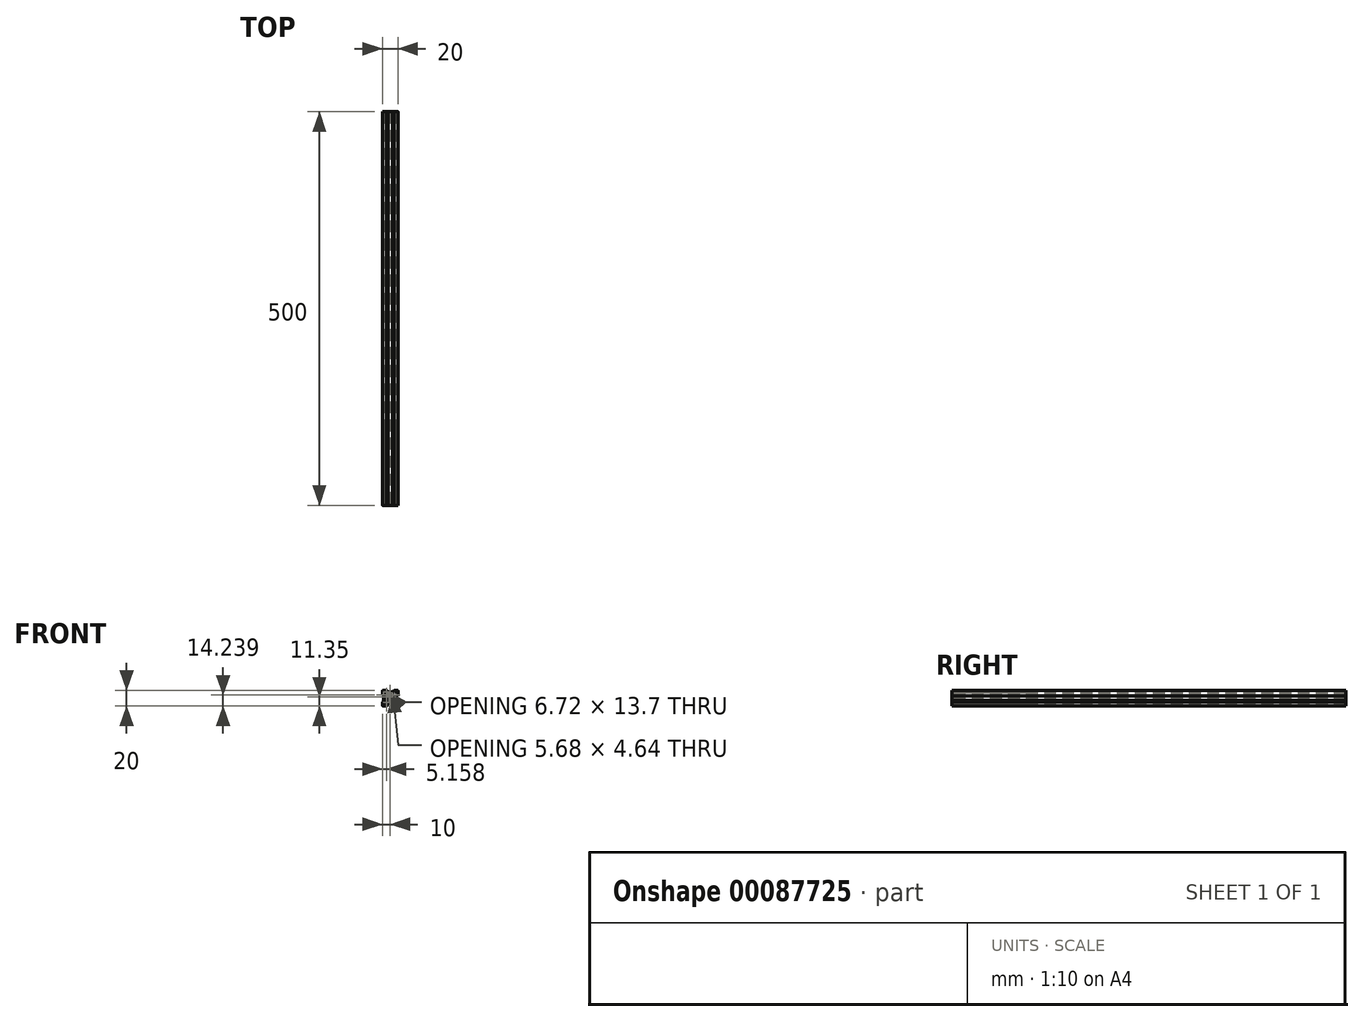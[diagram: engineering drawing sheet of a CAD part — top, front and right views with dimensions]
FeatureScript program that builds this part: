
annotation { "Feature Type Name" : "Feature", "Feature Type Description" : "" }
export const myFeature = defineFeature(function(context is Context, id is Id, definition is map)
    precondition{}
    {
        {
            var Q0;
            Q0=qCreatedBy(makeId("Front.planeOp"),FACE);
            var sketch = newSketch(context, id + "F0", { "sketchPlane" : qUnion([Q0])});
            skLineSegment(sketch, "E0.bottom", {"start": v(0, 0) * mm, "end": v(20, 0) * mm});
            skLineSegment(sketch, "E0.top", {"start": v(0, 20) * mm, "end": v(20, 20) * mm});
            skLineSegment(sketch, "E0.left", {"start": v(0, 0) * mm, "end": v(0, 20) * mm});
            skLineSegment(sketch, "E0.right", {"start": v(20, 0) * mm, "end": v(20, 20) * mm});
            skSolve(sketch);
        }
        {
            var Q0;
            Q0=makeQuery(id+"F0.imprint","IMPRINT",FACE,{"disambiguationData":[TD([[makeQuery(id+"F0.imprint","IMPRINT",EDGE,{"derivedFrom":sQuery(id+"F0.wireOp",EDGE,"E0.bottom")}),1.0]])]});
            extrude(context, id + "F1", {"entities" : qUnion([Q0]), "depth" : 500 * mm});
        }
        {
            var Q0;
            Q0=makeQuery(id+"F1.opExtrude","CAP_FACE",FACE,{"disambiguationData":[OSD([sQuery(id+"F0.wireOp",EDGE,"E0.bottom"),sQuery(id+"F0.wireOp",EDGE,"E0.top"),sQuery(id+"F0.wireOp",EDGE,"E0.left"),sQuery(id+"F0.wireOp",EDGE,"E0.right")])],"isStart":false});
            var sketch = newSketch(context, id + "F2", { "sketchPlane" : qUnion([Q0])});
            skCircle(sketch, "E1", {"center": v(10, 10) * mm, "radius": 2.1 * mm});
            skLineSegment(sketch, "E2", {"start": v(0, 18.94) * mm, "end": v(18.94, 0) * mm});
            skLineSegment(sketch, "E3", {"start": v(20, 1.06) * mm, "end": v(1.06, 20) * mm});
            skLineSegment(sketch, "E4.MirrorCS", {"start": v(20, 18.94) * mm, "end": v(1.06, 0) * mm});
            skLineSegment(sketch, "E5.MirrorCS", {"start": v(0, 1.06) * mm, "end": v(18.94, 20) * mm});
            skLineSegment(sketch, "E6", {"start": v(18.2, 1.8) * mm, "end": v(18.2, 18.2) * mm});
            skLineSegment(sketch, "E7.bottom", {"start": v(1.8, 18.2) * mm, "end": v(18.2, 18.2) * mm});
            skLineSegment(sketch, "E7.left", {"start": v(1.8, 18.2) * mm, "end": v(1.8, 1.8) * mm});
            skLineSegment(sketch, "E7.right", {"start": v(18.2, 18.2) * mm, "end": v(18.2, 1.8) * mm});
            skLineSegment(sketch, "E8", {"start": v(1.8, 1.8) * mm, "end": v(18.2, 1.8) * mm});
            skLineSegment(sketch, "E9", {"start": v(10, 10) * mm, "end": v(10, 0) * mm});
            skLineSegment(sketch, "E10", {"start": v(10, 0) * mm, "end": v(7.16, 0) * mm});
            skLineSegment(sketch, "E11", {"start": v(10, 0) * mm, "end": v(12.84, 0) * mm});
            skLineSegment(sketch, "E12", {"start": v(7.16, 0) * mm, "end": v(7.16, 6.1) * mm});
            skLineSegment(sketch, "E13", {"start": v(12.84, 0) * mm, "end": v(12.84, 6.1) * mm});
            skLineSegment(sketch, "E14", {"start": v(12.84, 6.1) * mm, "end": v(7.16, 6.1) * mm});
            skLineSegment(sketch, "E15", {"start": v(7.16, 1.8) * mm, "end": v(5.36, 0) * mm});
            skLineSegment(sketch, "E16", {"start": v(12.84, 0) * mm, "end": v(14.64, 0) * mm});
            skLineSegment(sketch, "E17", {"start": v(14.64, 0) * mm, "end": v(12.84, 1.8) * mm});
            skLineSegment(sketch, "E18", {"start": v(7.16, 1.8) * mm, "end": v(7.16, 3.44) * mm});
            skLineSegment(sketch, "E19", {"start": v(4.5, 3.44) * mm, "end": v(15.5, 3.44) * mm});
            skLineSegment(sketch, "E20", {"start": v(15.5, 3.44) * mm, "end": v(15.5, 0) * mm});
            skLineSegment(sketch, "E21", {"start": v(4.5, 3.44) * mm, "end": v(4.5, 0) * mm});
            skLineSegment(sketch, "E22.MirrorCS", {"start": v(14.64, 20) * mm, "end": v(12.84, 18.2) * mm});
            skLineSegment(sketch, "E23.MirrorCS", {"start": v(15.5, 16.56) * mm, "end": v(15.5, 20) * mm});
            skLineSegment(sketch, "E24.MirrorCS", {"start": v(7.16, 20) * mm, "end": v(7.16, 13.9) * mm});
            skLineSegment(sketch, "E25.MirrorCS", {"start": v(4.5, 16.56) * mm, "end": v(4.5, 20) * mm});
            skLineSegment(sketch, "E26.MirrorCS", {"start": v(10, 10) * mm, "end": v(10, 20) * mm});
            skLineSegment(sketch, "E27.MirrorCS", {"start": v(12.84, 13.9) * mm, "end": v(7.16, 13.9) * mm});
            skLineSegment(sketch, "E28.MirrorCS", {"start": v(12.84, 20) * mm, "end": v(14.64, 20) * mm});
            skLineSegment(sketch, "E29.MirrorCS", {"start": v(10, 20) * mm, "end": v(12.84, 20) * mm});
            skLineSegment(sketch, "E30.MirrorCS", {"start": v(10, 20) * mm, "end": v(7.16, 20) * mm});
            skLineSegment(sketch, "E31.MirrorCS", {"start": v(1.8, 1.8) * mm, "end": v(1.8, 18.2) * mm});
            skLineSegment(sketch, "E32.MirrorCS", {"start": v(12.84, 20) * mm, "end": v(12.84, 13.9) * mm});
            skLineSegment(sketch, "E33.MirrorCS", {"start": v(4.5, 16.56) * mm, "end": v(15.5, 16.56) * mm});
            skLineSegment(sketch, "E34.MirrorCS", {"start": v(7.16, 18.2) * mm, "end": v(5.36, 20) * mm});
            skLineSegment(sketch, "E35.MirrorCS", {"start": v(12.84, 1.8) * mm, "end": v(12.84, 3.44) * mm});
            skLineSegment(sketch, "E36.MirrorCS", {"start": v(12.84, 18.2) * mm, "end": v(12.84, 16.56) * mm});
            skLineSegment(sketch, "E37.MirrorCS", {"start": v(12.84, 1.8) * mm, "end": v(14.64, 0) * mm});
            skLineSegment(sketch, "E38.MirrorCS", {"start": v(12.84, 18.2) * mm, "end": v(14.64, 20) * mm});
            skLineSegment(sketch, "E39.MirrorCS", {"start": v(7.16, 6.1) * mm, "end": v(12.84, 6.1) * mm});
            skLineSegment(sketch, "E40.MirrorCS", {"start": v(15.5, 3.44) * mm, "end": v(4.5, 3.44) * mm});
            skLineSegment(sketch, "E41.MirrorCS", {"start": v(18.2, 1.8) * mm, "end": v(1.8, 1.8) * mm});
            skLineSegment(sketch, "E42.MirrorCS", {"start": v(7.16, 0) * mm, "end": v(5.36, 0) * mm});
            skLineSegment(sketch, "E43.MirrorCS", {"start": v(5.36, 0) * mm, "end": v(7.16, 1.8) * mm});
            skLineSegment(sketch, "E44", {"start": v(0, 20) * mm, "end": v(20, 0) * mm});
            skLineSegment(sketch, "E45.MirrorCS", {"start": v(3.44, 4.5) * mm, "end": v(0, 4.5) * mm});
            skLineSegment(sketch, "E46.MirrorCS", {"start": v(0, 10) * mm, "end": v(0, 7.16) * mm});
            skLineSegment(sketch, "E47.MirrorCS", {"start": v(0, 5.36) * mm, "end": v(1.8, 7.16) * mm});
            skLineSegment(sketch, "E48.MirrorCS", {"start": v(0, 7.16) * mm, "end": v(6.1, 7.16) * mm});
            skLineSegment(sketch, "E49.MirrorCS", {"start": v(1.8, 7.16) * mm, "end": v(3.44, 7.16) * mm});
            skLineSegment(sketch, "E50.MirrorCS", {"start": v(3.44, 15.5) * mm, "end": v(0, 15.5) * mm});
            skLineSegment(sketch, "E51.MirrorCS", {"start": v(0, 10) * mm, "end": v(0, 12.84) * mm});
            skLineSegment(sketch, "E52.MirrorCS", {"start": v(1.8, 12.84) * mm, "end": v(0, 14.64) * mm});
            skLineSegment(sketch, "E53.MirrorCS", {"start": v(0, 7.16) * mm, "end": v(0, 5.36) * mm});
            skLineSegment(sketch, "E54.MirrorCS", {"start": v(0, 12.84) * mm, "end": v(6.1, 12.84) * mm});
            skLineSegment(sketch, "E55.MirrorCS", {"start": v(6.1, 7.16) * mm, "end": v(6.1, 12.84) * mm});
            skLineSegment(sketch, "E56.MirrorCS", {"start": v(1.8, 7.16) * mm, "end": v(0, 5.36) * mm});
            skLineSegment(sketch, "E57.MirrorCS", {"start": v(1.8, 12.84) * mm, "end": v(3.44, 12.84) * mm});
            skLineSegment(sketch, "E58.MirrorCS", {"start": v(3.44, 15.5) * mm, "end": v(3.44, 4.5) * mm});
            skLineSegment(sketch, "E59.MirrorCS", {"start": v(18.2, 18.2) * mm, "end": v(1.8, 18.2) * mm});
            skLineSegment(sketch, "E60.MirrorCS", {"start": v(7.16, 18.2) * mm, "end": v(7.16, 16.56) * mm});
            skLineSegment(sketch, "E61.MirrorCS", {"start": v(18.2, 12.84) * mm, "end": v(16.56, 12.84) * mm});
            skLineSegment(sketch, "E62.MirrorCS", {"start": v(20, 7.16) * mm, "end": v(13.9, 7.16) * mm});
            skLineSegment(sketch, "E63.MirrorCS", {"start": v(18.2, 7.16) * mm, "end": v(16.56, 7.16) * mm});
            skLineSegment(sketch, "E64.MirrorCS", {"start": v(20, 12.84) * mm, "end": v(13.9, 12.84) * mm});
            skLineSegment(sketch, "E65.MirrorCS", {"start": v(16.56, 15.5) * mm, "end": v(20, 15.5) * mm});
            skLineSegment(sketch, "E66.MirrorCS", {"start": v(20, 14.64) * mm, "end": v(18.2, 12.84) * mm});
            skLineSegment(sketch, "E67.MirrorCS", {"start": v(20, 10) * mm, "end": v(20, 12.84) * mm});
            skLineSegment(sketch, "E68.MirrorCS", {"start": v(16.56, 4.5) * mm, "end": v(20, 4.5) * mm});
            skLineSegment(sketch, "E69.MirrorCS", {"start": v(20, 10) * mm, "end": v(20, 7.16) * mm});
            skLineSegment(sketch, "E70.MirrorCS", {"start": v(18.2, 7.16) * mm, "end": v(20, 5.36) * mm});
            skLineSegment(sketch, "E71.MirrorCS", {"start": v(13.9, 12.84) * mm, "end": v(13.9, 7.16) * mm});
            skLineSegment(sketch, "E72.MirrorCS", {"start": v(20, 5.36) * mm, "end": v(18.2, 7.16) * mm});
            skLineSegment(sketch, "E73.MirrorCS", {"start": v(16.56, 4.5) * mm, "end": v(16.56, 15.5) * mm});
            skLineSegment(sketch, "E74.MirrorCS", {"start": v(18.2, 12.84) * mm, "end": v(20, 14.64) * mm});
            skLineSegment(sketch, "E75.MirrorCS", {"start": v(13.9, 7.16) * mm, "end": v(13.9, 12.84) * mm});
            skLineSegment(sketch, "E76.MirrorCS", {"start": v(20, 7.16) * mm, "end": v(20, 5.36) * mm});
            skLineSegment(sketch, "E77.MirrorCS", {"start": v(16.56, 15.5) * mm, "end": v(16.56, 4.5) * mm});
            skLineSegment(sketch, "E78.MirrorCS", {"start": v(20, 12.84) * mm, "end": v(20, 14.64) * mm});
            skLineSegment(sketch, "E79", {"start": v(7.16, 18.2) * mm, "end": v(4.5, 18.2) * mm});
            skSolve(sketch);
        }
        {
            var Q0;
            {var subQ0=sQuery(id+"F2.wireOp",EDGE,"E55.MirrorCS");Q0=makeQuery(id+"F2.imprint","IMPRINT",FACE,{"disambiguationData":[TD([[makeQuery(id+"F2.imprint","IMPRINT",EDGE,{"derivedFrom":subQ0}),1.0]])]});}
            var Q1;
            {var subQ0=sQuery(id+"F2.wireOp",EDGE,"E58.MirrorCS");var subQ1=sQuery(id+"F2.wireOp",EDGE,"E2");var subQ2=makeQuery(id+"F2.imprint","INTERSECT",VERTEX,{"derivedFrom":[subQ1,sQuery(id+"F2.wireOp",EDGE,"E50.MirrorCS"),subQ0]});Q1=makeQuery(id+"F2.imprint","IMPRINT",FACE,{"disambiguationData":[TD([[makeQuery(id+"F2.imprint","IMPRINT",EDGE,{"disambiguationData":[TD([[subQ2,-1.0]])],"derivedFrom":subQ1}),-1.0]])]});}
            var Q2;
            {var subQ5=sQuery(id+"F2.wireOp",EDGE,"E57.MirrorCS");Q2=makeQuery(id+"F2.imprint","IMPRINT",FACE,{"disambiguationData":[TD([[makeQuery(id+"F2.imprint","IMPRINT",EDGE,{"derivedFrom":subQ5}),1.0]])]});}
            var Q3;
            {var subQ0=sQuery(id+"F2.wireOp",EDGE,"E57.MirrorCS");Q3=makeQuery(id+"F2.imprint","IMPRINT",FACE,{"disambiguationData":[TD([[makeQuery(id+"F2.imprint","IMPRINT",EDGE,{"derivedFrom":subQ0}),-1.0]])]});}
            var Q4;
            {var subQ4=sQuery(id+"F2.wireOp",EDGE,"E46.MirrorCS");Q4=makeQuery(id+"F2.imprint","IMPRINT",FACE,{"disambiguationData":[TD([[makeQuery(id+"F2.imprint","IMPRINT",EDGE,{"derivedFrom":subQ4}),-1.0]])]});}
            var Q5;
            {var subQ0=sQuery(id+"F2.wireOp",EDGE,"E52.MirrorCS");Q5=makeQuery(id+"F2.imprint","IMPRINT",FACE,{"disambiguationData":[TD([[makeQuery(id+"F2.imprint","IMPRINT",EDGE,{"derivedFrom":subQ0}),1.0]])]});}
            var Q6;
            {var subQ0=sQuery(id+"F2.wireOp",EDGE,"E53.MirrorCS");Q6=makeQuery(id+"F2.imprint","IMPRINT",FACE,{"disambiguationData":[TD([[makeQuery(id+"F2.imprint","IMPRINT",EDGE,{"derivedFrom":subQ0}),-1.0]])]});}
            var Q7;
            {var subQ1=sQuery(id+"F2.wireOp",EDGE,"E45.MirrorCS");var subQ3=sQuery(id+"F2.wireOp",EDGE,"E7.left");var subQ4=makeQuery(id+"F2.imprint","INTERSECT",VERTEX,{"derivedFrom":[subQ1,subQ3]});Q7=makeQuery(id+"F2.imprint","IMPRINT",FACE,{"disambiguationData":[TD([[makeQuery(id+"F2.imprint","IMPRINT",EDGE,{"disambiguationData":[TD([[subQ4,1.0]])],"derivedFrom":subQ1}),-1.0]])]});}
            var Q8;
            {var subQ0=sQuery(id+"F2.wireOp",EDGE,"E58.MirrorCS");var subQ3=sQuery(id+"F2.wireOp",EDGE,"E48.MirrorCS");var subQ5=makeQuery(id+"F2.imprint","INTERSECT",VERTEX,{"derivedFrom":[subQ0,subQ3]});Q8=makeQuery(id+"F2.imprint","IMPRINT",FACE,{"disambiguationData":[TD([[makeQuery(id+"F2.imprint","IMPRINT",EDGE,{"disambiguationData":[TD([[subQ5,-1.0]])],"derivedFrom":subQ0}),1.0]])]});}
            var Q9;
            {var subQ0=sQuery(id+"F2.wireOp",EDGE,"E27.MirrorCS");var subQ5=sQuery(id+"F2.wireOp",EDGE,"E26.MirrorCS");var subQ6=makeQuery(id+"F2.imprint","INTERSECT",VERTEX,{"derivedFrom":[subQ5,subQ0]});Q9=makeQuery(id+"F2.imprint","IMPRINT",FACE,{"disambiguationData":[TD([[makeQuery(id+"F2.imprint","IMPRINT",EDGE,{"disambiguationData":[TD([[subQ6,-1.0]])],"derivedFrom":subQ5}),1.0]])]});}
            var Q10;
            {var subQ0=sQuery(id+"F2.wireOp",EDGE,"E24.MirrorCS");var subQ1=sQuery(id+"F2.wireOp",EDGE,"E3");var subQ2=makeQuery(id+"F2.imprint","INTERSECT",VERTEX,{"derivedFrom":[subQ1,subQ0,sQuery(id+"F2.wireOp",EDGE,"E27.MirrorCS")]});Q10=makeQuery(id+"F2.imprint","IMPRINT",FACE,{"disambiguationData":[TD([[makeQuery(id+"F2.imprint","IMPRINT",EDGE,{"disambiguationData":[TD([[subQ2,-1.0]])],"derivedFrom":subQ1}),-1.0]])]});}
            var Q11;
            {var subQ0=sQuery(id+"F2.wireOp",EDGE,"E27.MirrorCS");var subQ1=sQuery(id+"F2.wireOp",EDGE,"E26.MirrorCS");var subQ2=makeQuery(id+"F2.imprint","INTERSECT",VERTEX,{"derivedFrom":[subQ1,subQ0]});Q11=makeQuery(id+"F2.imprint","IMPRINT",FACE,{"disambiguationData":[TD([[makeQuery(id+"F2.imprint","IMPRINT",EDGE,{"disambiguationData":[TD([[subQ2,-1.0]])],"derivedFrom":subQ1}),-1.0]])]});}
            var Q12;
            {var subQ0=sQuery(id+"F2.wireOp",EDGE,"E32.MirrorCS");var subQ1=sQuery(id+"F2.wireOp",EDGE,"E5.MirrorCS");var subQ2=makeQuery(id+"F2.imprint","INTERSECT",VERTEX,{"derivedFrom":[sQuery(id+"F2.wireOp",EDGE,"E27.MirrorCS"),subQ1,subQ0]});Q12=makeQuery(id+"F2.imprint","IMPRINT",FACE,{"disambiguationData":[TD([[makeQuery(id+"F2.imprint","IMPRINT",EDGE,{"disambiguationData":[TD([[subQ2,-1.0]])],"derivedFrom":subQ1}),1.0]])]});}
            var Q13;
            {var subQ0=sQuery(id+"F2.wireOp",EDGE,"E36.MirrorCS");Q13=makeQuery(id+"F2.imprint","IMPRINT",FACE,{"disambiguationData":[TD([[makeQuery(id+"F2.imprint","IMPRINT",EDGE,{"derivedFrom":subQ0}),1.0]])]});}
            var Q14;
            {var subQ5=sQuery(id+"F2.wireOp",EDGE,"E36.MirrorCS");Q14=makeQuery(id+"F2.imprint","IMPRINT",FACE,{"disambiguationData":[TD([[makeQuery(id+"F2.imprint","IMPRINT",EDGE,{"derivedFrom":subQ5}),-1.0]])]});}
            var Q15;
            {var subQ5=sQuery(id+"F2.wireOp",EDGE,"E60.MirrorCS");Q15=makeQuery(id+"F2.imprint","IMPRINT",FACE,{"disambiguationData":[TD([[makeQuery(id+"F2.imprint","IMPRINT",EDGE,{"derivedFrom":subQ5}),1.0]])]});}
            var Q16;
            {var subQ0=sQuery(id+"F2.wireOp",EDGE,"E60.MirrorCS");Q16=makeQuery(id+"F2.imprint","IMPRINT",FACE,{"disambiguationData":[TD([[makeQuery(id+"F2.imprint","IMPRINT",EDGE,{"derivedFrom":subQ0}),-1.0]])]});}
            var Q17;
            {var subQ3=sQuery(id+"F2.wireOp",EDGE,"E34.MirrorCS");Q17=makeQuery(id+"F2.imprint","IMPRINT",FACE,{"disambiguationData":[TD([[makeQuery(id+"F2.imprint","IMPRINT",EDGE,{"derivedFrom":subQ3}),-1.0]])]});}
            var Q18;
            {var subQ0=sQuery(id+"F2.wireOp",EDGE,"E30.MirrorCS");Q18=makeQuery(id+"F2.imprint","IMPRINT",FACE,{"disambiguationData":[TD([[makeQuery(id+"F2.imprint","IMPRINT",EDGE,{"derivedFrom":subQ0}),-1.0]])]});}
            var Q19;
            {var subQ0=sQuery(id+"F2.wireOp",EDGE,"E29.MirrorCS");Q19=makeQuery(id+"F2.imprint","IMPRINT",FACE,{"disambiguationData":[TD([[makeQuery(id+"F2.imprint","IMPRINT",EDGE,{"derivedFrom":subQ0}),-1.0]])]});}
            var Q20;
            {var subQ2=sQuery(id+"F2.wireOp",EDGE,"E22.MirrorCS");Q20=makeQuery(id+"F2.imprint","IMPRINT",FACE,{"disambiguationData":[TD([[makeQuery(id+"F2.imprint","IMPRINT",EDGE,{"derivedFrom":subQ2}),-1.0]])]});}
            var Q21;
            {var subQ0=sQuery(id+"F2.wireOp",EDGE,"E64.MirrorCS");var subQ3=sQuery(id+"F2.wireOp",EDGE,"E77.MirrorCS");var subQ5=makeQuery(id+"F2.imprint","INTERSECT",VERTEX,{"derivedFrom":[subQ3,subQ0]});Q21=makeQuery(id+"F2.imprint","IMPRINT",FACE,{"disambiguationData":[TD([[makeQuery(id+"F2.imprint","IMPRINT",EDGE,{"disambiguationData":[TD([[subQ5,1.0]])],"derivedFrom":subQ3}),-1.0]])]});}
            var Q22;
            {var subQ0=sQuery(id+"F2.wireOp",EDGE,"E75.MirrorCS");Q22=makeQuery(id+"F2.imprint","IMPRINT",FACE,{"disambiguationData":[TD([[makeQuery(id+"F2.imprint","IMPRINT",EDGE,{"derivedFrom":subQ0}),-1.0]])]});}
            var Q23;
            {var subQ0=sQuery(id+"F2.wireOp",EDGE,"E63.MirrorCS");Q23=makeQuery(id+"F2.imprint","IMPRINT",FACE,{"disambiguationData":[TD([[makeQuery(id+"F2.imprint","IMPRINT",EDGE,{"derivedFrom":subQ0}),-1.0]])]});}
            var Q24;
            {var subQ1=sQuery(id+"F2.wireOp",EDGE,"E77.MirrorCS");var subQ3=sQuery(id+"F2.wireOp",EDGE,"E64.MirrorCS");var subQ4=makeQuery(id+"F2.imprint","INTERSECT",VERTEX,{"derivedFrom":[subQ1,subQ3]});Q24=makeQuery(id+"F2.imprint","IMPRINT",FACE,{"disambiguationData":[TD([[makeQuery(id+"F2.imprint","IMPRINT",EDGE,{"disambiguationData":[TD([[subQ4,1.0]])],"derivedFrom":subQ1}),1.0]])]});}
            var Q25;
            {var subQ0=sQuery(id+"F2.wireOp",EDGE,"E74.MirrorCS");Q25=makeQuery(id+"F2.imprint","IMPRINT",FACE,{"disambiguationData":[TD([[makeQuery(id+"F2.imprint","IMPRINT",EDGE,{"derivedFrom":subQ0}),-1.0]])]});}
            var Q26;
            {var subQ6=sQuery(id+"F2.wireOp",EDGE,"E67.MirrorCS");Q26=makeQuery(id+"F2.imprint","IMPRINT",FACE,{"disambiguationData":[TD([[makeQuery(id+"F2.imprint","IMPRINT",EDGE,{"derivedFrom":subQ6}),1.0]])]});}
            var Q27;
            {var subQ0=sQuery(id+"F2.wireOp",EDGE,"E76.MirrorCS");Q27=makeQuery(id+"F2.imprint","IMPRINT",FACE,{"disambiguationData":[TD([[makeQuery(id+"F2.imprint","IMPRINT",EDGE,{"derivedFrom":subQ0}),1.0]])]});}
            var Q28;
            {var subQ3=sQuery(id+"F2.wireOp",EDGE,"E63.MirrorCS");Q28=makeQuery(id+"F2.imprint","IMPRINT",FACE,{"disambiguationData":[TD([[makeQuery(id+"F2.imprint","IMPRINT",EDGE,{"derivedFrom":subQ3}),1.0]])]});}
            var Q29;
            {var subQ0=sQuery(id+"F2.wireOp",EDGE,"E62.MirrorCS");var subQ1=sQuery(id+"F2.wireOp",EDGE,"E3");var subQ2=makeQuery(id+"F2.imprint","INTERSECT",VERTEX,{"derivedFrom":[subQ1,sQuery(id+"F2.wireOp",EDGE,"E75.MirrorCS"),subQ0]});Q29=makeQuery(id+"F2.imprint","IMPRINT",FACE,{"disambiguationData":[TD([[makeQuery(id+"F2.imprint","IMPRINT",EDGE,{"disambiguationData":[TD([[subQ2,1.0]])],"derivedFrom":subQ1}),-1.0]])]});}
            var Q30;
            {var subQ0=sQuery(id+"F2.wireOp",EDGE,"E16");Q30=makeQuery(id+"F2.imprint","IMPRINT",FACE,{"disambiguationData":[TD([[makeQuery(id+"F2.imprint","IMPRINT",EDGE,{"derivedFrom":subQ0}),1.0]])]});}
            var Q31;
            {var subQ0=sQuery(id+"F2.wireOp",EDGE,"E11");Q31=makeQuery(id+"F2.imprint","IMPRINT",FACE,{"disambiguationData":[TD([[makeQuery(id+"F2.imprint","IMPRINT",EDGE,{"derivedFrom":subQ0}),1.0]])]});}
            var Q32;
            {var subQ0=sQuery(id+"F2.wireOp",EDGE,"E10");Q32=makeQuery(id+"F2.imprint","IMPRINT",FACE,{"disambiguationData":[TD([[makeQuery(id+"F2.imprint","IMPRINT",EDGE,{"derivedFrom":subQ0}),1.0]])]});}
            var Q33;
            {var subQ0=sQuery(id+"F2.wireOp",EDGE,"E42.MirrorCS");Q33=makeQuery(id+"F2.imprint","IMPRINT",FACE,{"disambiguationData":[TD([[makeQuery(id+"F2.imprint","IMPRINT",EDGE,{"derivedFrom":subQ0}),1.0]])]});}
            var Q34;
            {var subQ1=sQuery(id+"F2.wireOp",EDGE,"E40.MirrorCS");var subQ3=sQuery(id+"F2.wireOp",EDGE,"E12");var subQ4=makeQuery(id+"F2.imprint","INTERSECT",VERTEX,{"derivedFrom":[subQ1,subQ3]});Q34=makeQuery(id+"F2.imprint","IMPRINT",FACE,{"disambiguationData":[TD([[makeQuery(id+"F2.imprint","IMPRINT",EDGE,{"disambiguationData":[TD([[subQ4,-1.0]])],"derivedFrom":subQ1}),1.0]])]});}
            var Q35;
            {var subQ0=sQuery(id+"F2.wireOp",EDGE,"E12");var subQ3=sQuery(id+"F2.wireOp",EDGE,"E40.MirrorCS");var subQ5=makeQuery(id+"F2.imprint","INTERSECT",VERTEX,{"derivedFrom":[subQ3,subQ0]});Q35=makeQuery(id+"F2.imprint","IMPRINT",FACE,{"disambiguationData":[TD([[makeQuery(id+"F2.imprint","IMPRINT",EDGE,{"disambiguationData":[TD([[subQ5,-1.0]])],"derivedFrom":subQ3}),-1.0]])]});}
            var Q36;
            {var subQ0=sQuery(id+"F2.wireOp",EDGE,"E39.MirrorCS");var subQ1=sQuery(id+"F2.wireOp",EDGE,"E9");var subQ2=makeQuery(id+"F2.imprint","INTERSECT",VERTEX,{"derivedFrom":[subQ1,subQ0]});Q36=makeQuery(id+"F2.imprint","IMPRINT",FACE,{"disambiguationData":[TD([[makeQuery(id+"F2.imprint","IMPRINT",EDGE,{"disambiguationData":[TD([[subQ2,-1.0]])],"derivedFrom":subQ1}),-1.0]])]});}
            var Q37;
            {var subQ0=sQuery(id+"F2.wireOp",EDGE,"E39.MirrorCS");var subQ1=sQuery(id+"F2.wireOp",EDGE,"E9");var subQ2=makeQuery(id+"F2.imprint","INTERSECT",VERTEX,{"derivedFrom":[subQ1,subQ0]});Q37=makeQuery(id+"F2.imprint","IMPRINT",FACE,{"disambiguationData":[TD([[makeQuery(id+"F2.imprint","IMPRINT",EDGE,{"disambiguationData":[TD([[subQ2,-1.0]])],"derivedFrom":subQ1}),1.0]])]});}
            var Q38;
            {var subQ0=sQuery(id+"F2.wireOp",EDGE,"E13");var subQ3=sQuery(id+"F2.wireOp",EDGE,"E40.MirrorCS");var subQ5=makeQuery(id+"F2.imprint","INTERSECT",VERTEX,{"derivedFrom":[subQ3,subQ0]});Q38=makeQuery(id+"F2.imprint","IMPRINT",FACE,{"disambiguationData":[TD([[makeQuery(id+"F2.imprint","IMPRINT",EDGE,{"disambiguationData":[TD([[subQ5,1.0]])],"derivedFrom":subQ3}),-1.0]])]});}
            var Q39;
            {var subQ1=sQuery(id+"F2.wireOp",EDGE,"E20");var subQ3=sQuery(id+"F2.wireOp",EDGE,"E41.MirrorCS");var subQ4=makeQuery(id+"F2.imprint","INTERSECT",VERTEX,{"derivedFrom":[subQ1,subQ3]});Q39=makeQuery(id+"F2.imprint","IMPRINT",FACE,{"disambiguationData":[TD([[makeQuery(id+"F2.imprint","IMPRINT",EDGE,{"disambiguationData":[TD([[subQ4,1.0]])],"derivedFrom":subQ1}),-1.0]])]});}
            var Q40;
            {var subQ0=sQuery(id+"F2.wireOp",EDGE,"E40.MirrorCS");var subQ1=sQuery(id+"F2.wireOp",EDGE,"E9");var subQ2=makeQuery(id+"F2.imprint","INTERSECT",VERTEX,{"derivedFrom":[subQ1,subQ0]});Q40=makeQuery(id+"F2.imprint","IMPRINT",FACE,{"disambiguationData":[TD([[makeQuery(id+"F2.imprint","IMPRINT",EDGE,{"disambiguationData":[TD([[subQ2,-1.0]])],"derivedFrom":subQ1}),1.0]])]});}
            var Q41;
            {var subQ0=sQuery(id+"F2.wireOp",EDGE,"E40.MirrorCS");var subQ1=sQuery(id+"F2.wireOp",EDGE,"E9");var subQ2=makeQuery(id+"F2.imprint","INTERSECT",VERTEX,{"derivedFrom":[subQ1,subQ0]});Q41=makeQuery(id+"F2.imprint","IMPRINT",FACE,{"disambiguationData":[TD([[makeQuery(id+"F2.imprint","IMPRINT",EDGE,{"disambiguationData":[TD([[subQ2,-1.0]])],"derivedFrom":subQ1}),-1.0]])]});}
            var Q42;
            {var subQ0=sQuery(id+"F2.wireOp",EDGE,"E2");var subQ1=sQuery(id+"F2.wireOp",EDGE,"E1");var subQ2=makeQuery(id+"F2.imprint","INTERSECT",VERTEX,{"disambiguationData":[OD(1.0)],"derivedFrom":[subQ1,subQ0]});Q42=makeQuery(id+"F2.imprint","IMPRINT",FACE,{"disambiguationData":[TD([[makeQuery(id+"F2.imprint","IMPRINT",EDGE,{"disambiguationData":[TD([[subQ2,-1.0]])],"derivedFrom":subQ1}),-1.0]])]});}
            var Q43;
            {var subQ0=sQuery(id+"F2.wireOp",EDGE,"E9");var subQ1=sQuery(id+"F2.wireOp",EDGE,"E1");var subQ2=makeQuery(id+"F2.imprint","INTERSECT",VERTEX,{"derivedFrom":[subQ1,subQ0]});Q43=makeQuery(id+"F2.imprint","IMPRINT",FACE,{"disambiguationData":[TD([[makeQuery(id+"F2.imprint","IMPRINT",EDGE,{"disambiguationData":[TD([[subQ2,-1.0]])],"derivedFrom":subQ1}),-1.0]])]});}
            var Q44;
            {var subQ0=sQuery(id+"F2.wireOp",EDGE,"E4.MirrorCS");var subQ1=sQuery(id+"F2.wireOp",EDGE,"E1");var subQ2=makeQuery(id+"F2.imprint","INTERSECT",VERTEX,{"disambiguationData":[OD(1.0)],"derivedFrom":[subQ1,subQ0]});Q44=makeQuery(id+"F2.imprint","IMPRINT",FACE,{"disambiguationData":[TD([[makeQuery(id+"F2.imprint","IMPRINT",EDGE,{"disambiguationData":[TD([[subQ2,-1.0]])],"derivedFrom":subQ1}),-1.0]])]});}
            var Q45;
            {var subQ0=sQuery(id+"F2.wireOp",EDGE,"E2");var subQ1=sQuery(id+"F2.wireOp",EDGE,"E1");var subQ2=makeQuery(id+"F2.imprint","INTERSECT",VERTEX,{"disambiguationData":[OD(0.0)],"derivedFrom":[subQ1,subQ0]});Q45=makeQuery(id+"F2.imprint","IMPRINT",FACE,{"disambiguationData":[TD([[makeQuery(id+"F2.imprint","IMPRINT",EDGE,{"disambiguationData":[TD([[subQ2,1.0]])],"derivedFrom":subQ1}),-1.0]])]});}
            var Q46;
            {var subQ0=sQuery(id+"F2.wireOp",EDGE,"E44");var subQ1=sQuery(id+"F2.wireOp",EDGE,"E1");var subQ2=makeQuery(id+"F2.imprint","INTERSECT",VERTEX,{"disambiguationData":[OD(0.0)],"derivedFrom":[subQ1,subQ0]});Q46=makeQuery(id+"F2.imprint","IMPRINT",FACE,{"disambiguationData":[TD([[makeQuery(id+"F2.imprint","IMPRINT",EDGE,{"disambiguationData":[TD([[subQ2,1.0]])],"derivedFrom":subQ1}),-1.0]])]});}
            var Q47;
            {var subQ0=sQuery(id+"F2.wireOp",EDGE,"E44");var subQ1=sQuery(id+"F2.wireOp",EDGE,"E1");var subQ2=makeQuery(id+"F2.imprint","INTERSECT",VERTEX,{"disambiguationData":[OD(0.0)],"derivedFrom":[subQ1,subQ0]});Q47=makeQuery(id+"F2.imprint","IMPRINT",FACE,{"disambiguationData":[TD([[makeQuery(id+"F2.imprint","IMPRINT",EDGE,{"disambiguationData":[TD([[subQ2,-1.0]])],"derivedFrom":subQ1}),-1.0]])]});}
            var Q48;
            {var subQ0=sQuery(id+"F2.wireOp",EDGE,"E3");var subQ1=sQuery(id+"F2.wireOp",EDGE,"E1");var subQ2=makeQuery(id+"F2.imprint","INTERSECT",VERTEX,{"disambiguationData":[OD(0.0)],"derivedFrom":[subQ1,subQ0]});Q48=makeQuery(id+"F2.imprint","IMPRINT",FACE,{"disambiguationData":[TD([[makeQuery(id+"F2.imprint","IMPRINT",EDGE,{"disambiguationData":[TD([[subQ2,-1.0]])],"derivedFrom":subQ1}),-1.0]])]});}
            var Q49;
            {var subQ0=sQuery(id+"F2.wireOp",EDGE,"E26.MirrorCS");var subQ1=sQuery(id+"F2.wireOp",EDGE,"E1");var subQ2=makeQuery(id+"F2.imprint","INTERSECT",VERTEX,{"derivedFrom":[subQ1,subQ0]});Q49=makeQuery(id+"F2.imprint","IMPRINT",FACE,{"disambiguationData":[TD([[makeQuery(id+"F2.imprint","IMPRINT",EDGE,{"disambiguationData":[TD([[subQ2,-1.0]])],"derivedFrom":subQ1}),-1.0]])]});}
            var Q50;
            {var subQ0=sQuery(id+"F2.wireOp",EDGE,"E5.MirrorCS");var subQ1=sQuery(id+"F2.wireOp",EDGE,"E1");var subQ2=makeQuery(id+"F2.imprint","INTERSECT",VERTEX,{"disambiguationData":[OD(0.0)],"derivedFrom":[subQ1,subQ0]});Q50=makeQuery(id+"F2.imprint","IMPRINT",FACE,{"disambiguationData":[TD([[makeQuery(id+"F2.imprint","IMPRINT",EDGE,{"disambiguationData":[TD([[subQ2,-1.0]])],"derivedFrom":subQ1}),-1.0]])]});}
            var Q51;
            {var subQ0=sQuery(id+"F2.wireOp",EDGE,"E4.MirrorCS");var subQ1=sQuery(id+"F2.wireOp",EDGE,"E1");var subQ2=makeQuery(id+"F2.imprint","INTERSECT",VERTEX,{"disambiguationData":[OD(0.0)],"derivedFrom":[subQ1,subQ0]});Q51=makeQuery(id+"F2.imprint","IMPRINT",FACE,{"disambiguationData":[TD([[makeQuery(id+"F2.imprint","IMPRINT",EDGE,{"disambiguationData":[TD([[subQ2,-1.0]])],"derivedFrom":subQ1}),-1.0]])]});}
            var Q52;
            {var subQ0=sQuery(id+"F2.wireOp",EDGE,"E3");var subQ1=sQuery(id+"F2.wireOp",EDGE,"E1");var subQ2=makeQuery(id+"F2.imprint","INTERSECT",VERTEX,{"disambiguationData":[OD(1.0)],"derivedFrom":[subQ1,subQ0]});Q52=makeQuery(id+"F2.imprint","IMPRINT",FACE,{"disambiguationData":[TD([[makeQuery(id+"F2.imprint","IMPRINT",EDGE,{"disambiguationData":[TD([[subQ2,-1.0]])],"derivedFrom":subQ1}),-1.0]])]});}
            var Q53;
            {var subQ0=sQuery(id+"F2.wireOp",EDGE,"E44");var subQ1=sQuery(id+"F2.wireOp",EDGE,"E1");var subQ2=makeQuery(id+"F2.imprint","INTERSECT",VERTEX,{"disambiguationData":[OD(1.0)],"derivedFrom":[subQ1,subQ0]});Q53=makeQuery(id+"F2.imprint","IMPRINT",FACE,{"disambiguationData":[TD([[makeQuery(id+"F2.imprint","IMPRINT",EDGE,{"disambiguationData":[TD([[subQ2,-1.0]])],"derivedFrom":subQ1}),-1.0]])]});}
            var Q54;
            {var subQ0=sQuery(id+"F2.wireOp",EDGE,"E5.MirrorCS");var subQ1=sQuery(id+"F2.wireOp",EDGE,"E2");var subQ2=makeQuery(id+"F2.imprint","INTERSECT",VERTEX,{"derivedFrom":[subQ1,subQ0]});Q54=makeQuery(id+"F2.imprint","IMPRINT",FACE,{"disambiguationData":[TD([[makeQuery(id+"F2.imprint","IMPRINT",EDGE,{"disambiguationData":[TD([[subQ2,-1.0]])],"derivedFrom":subQ0}),-1.0]])]});}
            var Q55;
            {var subQ0=sQuery(id+"F2.wireOp",EDGE,"E4.MirrorCS");var subQ1=sQuery(id+"F2.wireOp",EDGE,"E3");var subQ2=makeQuery(id+"F2.imprint","INTERSECT",VERTEX,{"derivedFrom":[subQ1,subQ0]});Q55=makeQuery(id+"F2.imprint","IMPRINT",FACE,{"disambiguationData":[TD([[makeQuery(id+"F2.imprint","IMPRINT",EDGE,{"disambiguationData":[TD([[subQ2,-1.0]])],"derivedFrom":subQ0}),-1.0]])]});}
            var Q56;
            {var subQ0=sQuery(id+"F2.wireOp",EDGE,"E44");var subQ1=sQuery(id+"F2.wireOp",EDGE,"E4.MirrorCS");var subQ2=makeQuery(id+"F2.imprint","INTERSECT",VERTEX,{"derivedFrom":[subQ1,subQ0]});Q56=makeQuery(id+"F2.imprint","IMPRINT",FACE,{"disambiguationData":[TD([[makeQuery(id+"F2.imprint","IMPRINT",EDGE,{"disambiguationData":[TD([[subQ2,-1.0]])],"derivedFrom":subQ1}),-1.0]])]});}
            var Q57;
            {var subQ0=sQuery(id+"F2.wireOp",EDGE,"E44");var subQ3=sQuery(id+"F2.wireOp",EDGE,"E5.MirrorCS");var subQ5=makeQuery(id+"F2.imprint","INTERSECT",VERTEX,{"derivedFrom":[subQ3,subQ0]});Q57=makeQuery(id+"F2.imprint","IMPRINT",FACE,{"disambiguationData":[TD([[makeQuery(id+"F2.imprint","IMPRINT",EDGE,{"disambiguationData":[TD([[subQ5,-1.0]])],"derivedFrom":subQ3}),-1.0]])]});}
            extrude(context, id + "F3", {"entities" : qUnion([Q0, Q1, Q2, Q3, Q4, Q5, Q6, Q7, Q8, Q9, Q10, Q11, Q12, Q13, Q14, Q15, Q16, Q17, Q18, Q19, Q20, Q21, Q22, Q23, Q24, Q25, Q26, Q27, Q28, Q29, Q30, Q31, Q32, Q33, Q34, Q35, Q36, Q37, Q38, Q39, Q40, Q41, Q42, Q43, Q44, Q45, Q46, Q47, Q48, Q49, Q50, Q51, Q52, Q53, Q54, Q55, Q56, Q57]), "operationType" : NewBodyOperationType.REMOVE, "oppositeDirection" : true, "depth" : 1000 * mm});
        }
        {
            var Q0;
            Q0=makeQuery(id+"F1.opExtrude","CAP_FACE",FACE,{"disambiguationData":[OSD([sQuery(id+"F0.wireOp",EDGE,"E0.bottom"),sQuery(id+"F0.wireOp",EDGE,"E0.top"),sQuery(id+"F0.wireOp",EDGE,"E0.left"),sQuery(id+"F0.wireOp",EDGE,"E0.right")])],"isStart":false});
            var sketch = newSketch(context, id + "F4", { "sketchPlane" : qUnion([Q0])});
            skLineSegment(sketch, "E80", {"start": v(1.8, 15.5) * mm, "end": v(1.8, 16.57) * mm});
            skLineSegment(sketch, "E81", {"start": v(4.5, 18.2) * mm, "end": v(3.43, 18.2) * mm});
            skLineSegment(sketch, "E82", {"start": v(1.8, 16.57) * mm, "end": v(3.43, 18.2) * mm});
            skLineSegment(sketch, "E83", {"start": v(3.43, 18.2) * mm, "end": v(1.8, 18.2) * mm});
            skLineSegment(sketch, "E84", {"start": v(1.8, 18.2) * mm, "end": v(1.8, 16.57) * mm});
            skLineSegment(sketch, "E85.bottom", {"start": v(0, 20) * mm, "end": v(20, 20) * mm});
            skLineSegment(sketch, "E85.top", {"start": v(0, 0) * mm, "end": v(20, 0) * mm});
            skLineSegment(sketch, "E85.left", {"start": v(0, 20) * mm, "end": v(0, 0) * mm});
            skLineSegment(sketch, "E85.right", {"start": v(20, 20) * mm, "end": v(20, 0) * mm});
            skLineSegment(sketch, "E86", {"start": v(0, 10) * mm, "end": v(20, 10) * mm});
            skLineSegment(sketch, "E87", {"start": v(10, 20) * mm, "end": v(10, 0) * mm});
            skLineSegment(sketch, "E88.MirrorCS", {"start": v(18.2, 16.57) * mm, "end": v(16.57, 18.2) * mm});
            skLineSegment(sketch, "E89.MirrorCS", {"start": v(16.57, 18.2) * mm, "end": v(18.2, 18.2) * mm});
            skLineSegment(sketch, "E90.MirrorCS", {"start": v(18.2, 18.2) * mm, "end": v(18.2, 16.57) * mm});
            skLineSegment(sketch, "E91.MirrorCS", {"start": v(18.2, 15.5) * mm, "end": v(18.2, 16.57) * mm});
            skLineSegment(sketch, "E92.MirrorCS", {"start": v(15.5, 18.2) * mm, "end": v(16.57, 18.2) * mm});
            skLineSegment(sketch, "E93.MirrorCS", {"start": v(18.2, 4.5) * mm, "end": v(18.2, 3.43) * mm});
            skLineSegment(sketch, "E94.MirrorCS", {"start": v(4.5, 1.8) * mm, "end": v(3.43, 1.8) * mm});
            skLineSegment(sketch, "E95.MirrorCS", {"start": v(3.43, 1.8) * mm, "end": v(1.8, 1.8) * mm});
            skLineSegment(sketch, "E96.MirrorCS", {"start": v(1.8, 1.8) * mm, "end": v(1.8, 3.43) * mm});
            skLineSegment(sketch, "E97.MirrorCS", {"start": v(18.2, 1.8) * mm, "end": v(18.2, 3.43) * mm});
            skLineSegment(sketch, "E98.MirrorCS", {"start": v(18.2, 3.43) * mm, "end": v(16.57, 1.8) * mm});
            skLineSegment(sketch, "E99.MirrorCS", {"start": v(15.5, 1.8) * mm, "end": v(16.57, 1.8) * mm});
            skLineSegment(sketch, "E100.MirrorCS", {"start": v(1.8, 4.5) * mm, "end": v(1.8, 3.43) * mm});
            skLineSegment(sketch, "E101.MirrorCS", {"start": v(1.8, 3.43) * mm, "end": v(3.43, 1.8) * mm});
            skLineSegment(sketch, "E102.MirrorCS", {"start": v(16.57, 1.8) * mm, "end": v(18.2, 1.8) * mm});
            skSolve(sketch);
        }
        {
            var Q0;
            Q0=makeQuery(id+"F4.imprint","IMPRINT",FACE,{"disambiguationData":[TD([[makeQuery(id+"F4.imprint","IMPRINT",EDGE,{"derivedFrom":sQuery(id+"F4.wireOp",EDGE,"E95.MirrorCS")}),-1.0]])]});
            var Q1;
            Q1=makeQuery(id+"F4.imprint","IMPRINT",FACE,{"disambiguationData":[TD([[makeQuery(id+"F4.imprint","IMPRINT",EDGE,{"derivedFrom":sQuery(id+"F4.wireOp",EDGE,"E82")}),1.0]])]});
            var Q2;
            Q2=makeQuery(id+"F4.imprint","IMPRINT",FACE,{"disambiguationData":[TD([[makeQuery(id+"F4.imprint","IMPRINT",EDGE,{"derivedFrom":sQuery(id+"F4.wireOp",EDGE,"E88.MirrorCS")}),-1.0]])]});
            var Q3;
            Q3=makeQuery(id+"F4.imprint","IMPRINT",FACE,{"disambiguationData":[TD([[makeQuery(id+"F4.imprint","IMPRINT",EDGE,{"derivedFrom":sQuery(id+"F4.wireOp",EDGE,"E97.MirrorCS")}),1.0]])]});
            extrude(context, id + "F5", {"entities" : qUnion([Q0, Q1, Q2, Q3]), "operationType" : NewBodyOperationType.REMOVE, "oppositeDirection" : true, "depth" : 100 * mm});
        }
        {
            var Q0;
            Q0=makeQuery(id+"F1.opExtrude","SWEPT_EDGE",EDGE,{"disambiguationData":[OSD([sQuery(id+"F0.wireOp",EDGE,"E0.top"),sQuery(id+"F0.wireOp",EDGE,"E0.right")])]});
            var Q1;
            Q1=makeQuery(id+"F1.opExtrude","SWEPT_EDGE",EDGE,{"disambiguationData":[OSD([sQuery(id+"F0.wireOp",EDGE,"E0.bottom"),sQuery(id+"F0.wireOp",EDGE,"E0.right")])]});
            var Q2;
            Q2=makeQuery(id+"F1.opExtrude","SWEPT_EDGE",EDGE,{"disambiguationData":[OSD([sQuery(id+"F0.wireOp",EDGE,"E0.top"),sQuery(id+"F0.wireOp",EDGE,"E0.left")])]});
            var Q3;
            Q3=makeQuery(id+"F1.opExtrude","SWEPT_EDGE",EDGE,{"disambiguationData":[OSD([sQuery(id+"F0.wireOp",EDGE,"E0.bottom"),sQuery(id+"F0.wireOp",EDGE,"E0.left")])]});
            fillet(context, id + "F6", {"entities" : qUnion([Q0, Q1, Q2, Q3]), "radius" : 1 * mm, "tangentPropagation" : true, "allowEdgeOverflow" : false});
        }
    });
